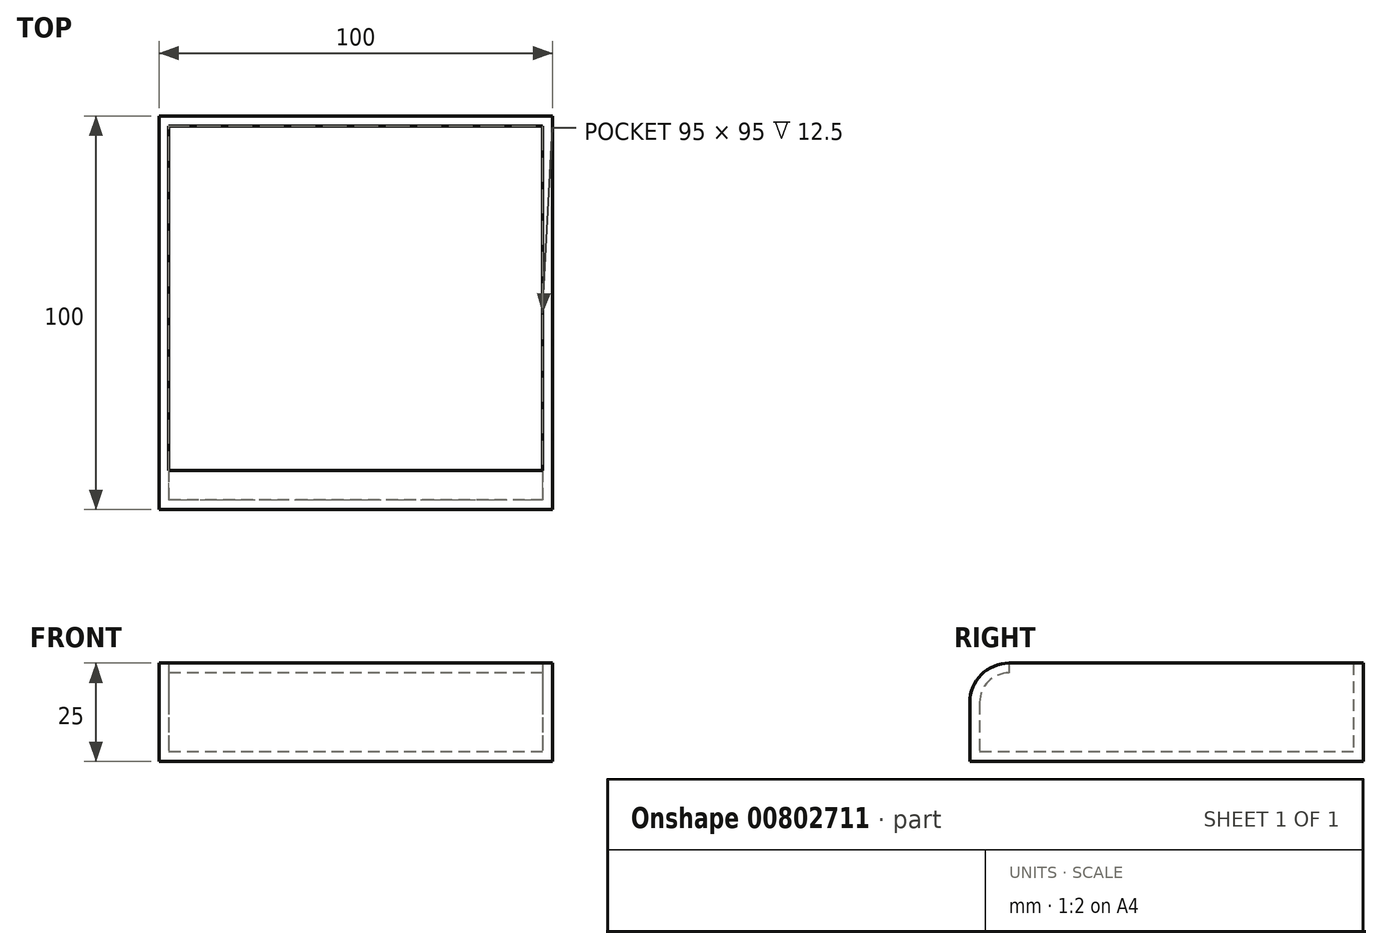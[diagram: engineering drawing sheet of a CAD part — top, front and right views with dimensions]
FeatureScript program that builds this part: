
annotation { "Feature Type Name" : "Feature", "Feature Type Description" : "" }
export const myFeature = defineFeature(function(context is Context, id is Id, definition is map)
    precondition{}
    {
        {
            var Q0;
            Q0=qCreatedBy(makeId("Top.planeOp"),FACE);
            var sketch = newSketch(context, id + "F0", { "sketchPlane" : qUnion([Q0])});
            skLineSegment(sketch, "E0.bottom", {"start": v(50, 50) * mm, "end": v(-50, 50) * mm});
            skLineSegment(sketch, "E0.top", {"start": v(50, -50) * mm, "end": v(-50, -50) * mm});
            skLineSegment(sketch, "E0.left", {"start": v(50, 50) * mm, "end": v(50, -50) * mm});
            skLineSegment(sketch, "E0.right", {"start": v(-50, 50) * mm, "end": v(-50, -50) * mm});
            skPoint(sketch, "E0.middle", {"position": v(0, 0) * mm});
            skSolve(sketch);
        }
        {
            var Q0;
            Q0 = qSketchRegion(id + "F0", true);
            extrude(context, id + "F1", {"entities" : qUnion([Q0]), "depth" : 25 * mm, "offsetDistance" : 25 * mm});
        }
        {
            var Q0;
            Q0=makeQuery(id+"F1.opExtrude","CAP_EDGE",EDGE,{"disambiguationData":[OSD([sQuery(id+"F0.wireOp",EDGE,"E0.top")])],"isStart":false});
            fillet(context, id + "F2", {"entities" : qUnion([Q0]), "radius" : 10 * mm, "tangentPropagation" : true, "allowEdgeOverflow" : false});
        }
        {
            var Q0;
            Q0=makeQuery(id+"F1.opExtrude","CAP_FACE",FACE,{"disambiguationData":[OSD([sQuery(id+"F0.wireOp",EDGE,"E0.bottom"),sQuery(id+"F0.wireOp",EDGE,"E0.top"),sQuery(id+"F0.wireOp",EDGE,"E0.left"),sQuery(id+"F0.wireOp",EDGE,"E0.right")])],"isStart":false});
            shell(context, id + "F3", {"entities" : qUnion([Q0]), "thickness" : 2.5 * mm});
        }
    });
